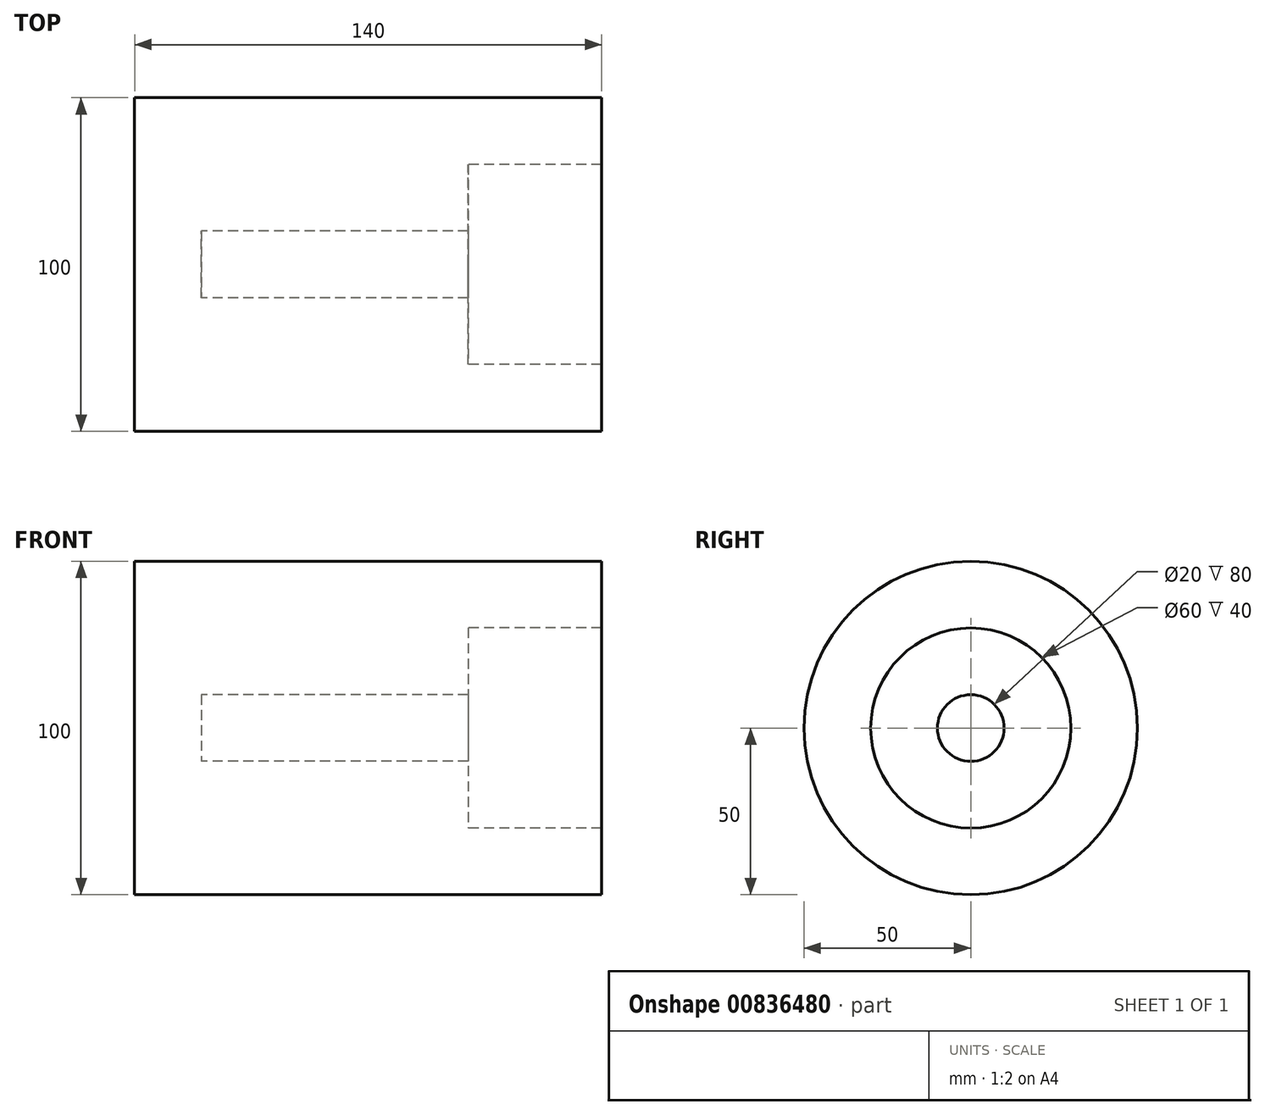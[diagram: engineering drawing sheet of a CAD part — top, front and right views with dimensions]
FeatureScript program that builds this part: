
annotation { "Feature Type Name" : "Feature", "Feature Type Description" : "" }
export const myFeature = defineFeature(function(context is Context, id is Id, definition is map)
    precondition{}
    {
        {
            var Q0;
            Q0=qCreatedBy(makeId("Top.planeOp"),FACE);
            var sketch = newSketch(context, id + "F0", { "sketchPlane" : qUnion([Q0])});
            skLineSegment(sketch, "E0", {"start": v(-64.32, 50) * mm, "end": v(75.68, 50) * mm});
            skLineSegment(sketch, "E1", {"start": v(75.68, 50) * mm, "end": v(75.68, 30) * mm});
            skLineSegment(sketch, "E2", {"start": v(75.68, 30) * mm, "end": v(35.68, 30) * mm});
            skLineSegment(sketch, "E3", {"start": v(35.68, 30) * mm, "end": v(35.68, 10) * mm});
            skLineSegment(sketch, "E4", {"start": v(35.68, 10) * mm, "end": v(-44.32, 10) * mm});
            skLineSegment(sketch, "E5", {"start": v(-64.32, 50) * mm, "end": v(-64.32, 0) * mm});
            skLineSegment(sketch, "E6", {"start": v(-64.32, 0) * mm, "end": v(-44.32, 0) * mm});
            skLineSegment(sketch, "E7", {"start": v(-44.32, 0) * mm, "end": v(-44.32, 10) * mm});
            skSolve(sketch);
        }
        {
            var Q0;
            Q0=makeQuery(id+"F0.imprint","IMPRINT",FACE,{"disambiguationData":[TD([[makeQuery(id+"F0.imprint","IMPRINT",EDGE,{"derivedFrom":sQuery(id+"F0.wireOp",EDGE,"E0")}),-1.0]])]});
            var Q1;
            Q1=sQuery(id+"F0.wireOp",EDGE,"E6");
            revolve(context, id + "F1", {"surfaceOperationType" : NewSurfaceOperationType.NEW, "entities" : qUnion([Q0]), "axis" : qUnion([Q1]), "revolveType" : RevolveType.FULL});
        }
    });
